# Revit family: Reece_Basin_Roca_The Gap_Semi Inset Basin_550 mm
name_source: partatom
category: Plumbing Fixtures
revit_build: Autodesk Revit 2018 (Build: 20181011_1500(x64)
units: mm (PartAtom-declared; Revit-internal decimal feet)

## family parameters
Cut with Voids When Loaded = No
Host = Face
Part Type = Normal
Room Calculation Point = Yes
Round Connector Dimension = Use Diameter
Shared = Yes

## types (1)
- 1 Taphole_Vitreous China
    CWFU = 0
    Default Elevation = 1000 mm  [stored 3.28084 ft]
    Description = Roca The Gap Semi Inset Basin 550mm x 410mm 1 Taphole White
    Disclaimer = THIS FILE IS THE PROPERTY OF THE REECE GROUP. IT MAY NOT BE REPRODUCED, REVERSE-ENGINEERED, OR MODIFIED. ANY REPUBLICATION, TRANSMISSION, OR DISTRIBUTION FOR THE PURPOSE OF COMMERCIALLY EXPLOITING THE FILES IS PROHIBITED.
    HWFU = 0
    Keynote = Product #9506765, Reece_Basin_Roca_The Gap_Semi Inset Basin_550 mm - 1 Taphole_Vitreous China
    Manufacturer = Roca
    Model = The Gap
    Reece_Basin_Outlet = 50 mm  [stored 0.164042 ft]
    Reece_Detail_Additional = Overflow
    Reece_Detail_Connector = 1 Taphole
    Reece_Detail_Disclaimer = THIS FILE IS THE PROPERTY OF THE REECE GROUP. IT MAY NOT BE REPRODUCED, REVERSE-ENGINEERED, OR MODIFIED. ANY REPUBLICATION, TRANSMISSION, OR DISTRIBUTION FOR THE PURPOSE OF COMMERCIALLY EXPLOITING THE FILES IS PROHIBITED.
    Reece_Detail_Installation = Semi Inset Basin
    Reece_Material_Main = Reece_Vitreous China_White
    Reece_Material_Secondary = Reece_Brass_Chrome
    Reece_Overall_Capacity = 6.4 L
    Reece_Overall_Height = 165 mm
    Reece_Overall_Length = 410 mm
    Reece_Overall_Width = 550 mm
    Reece_Product_Brand = Roca
    Reece_Product_Description = Roca The Gap Semi Inset Basin 550mm x 410mm 1 Taphole White
    Reece_Product_Mount = Semi Inset
    Reece_Product_Number = 9506765
    Reece_Product_Sub Brand = The Gap
    Reece_Product_Type = Basin
    Reece_Product_Web Page = https://www.reece.com.au
    Type Comments = Basin
    URL = https://www.reece.com.au
    WFU = 0

note: [stored X ft] marks values corroborated as IEEE doubles in the binary element streams (Revit-internal decimal feet)

## geometry (parser evidence)
native form markers: Sweep x3
no freeform markers — native parametric forms only
